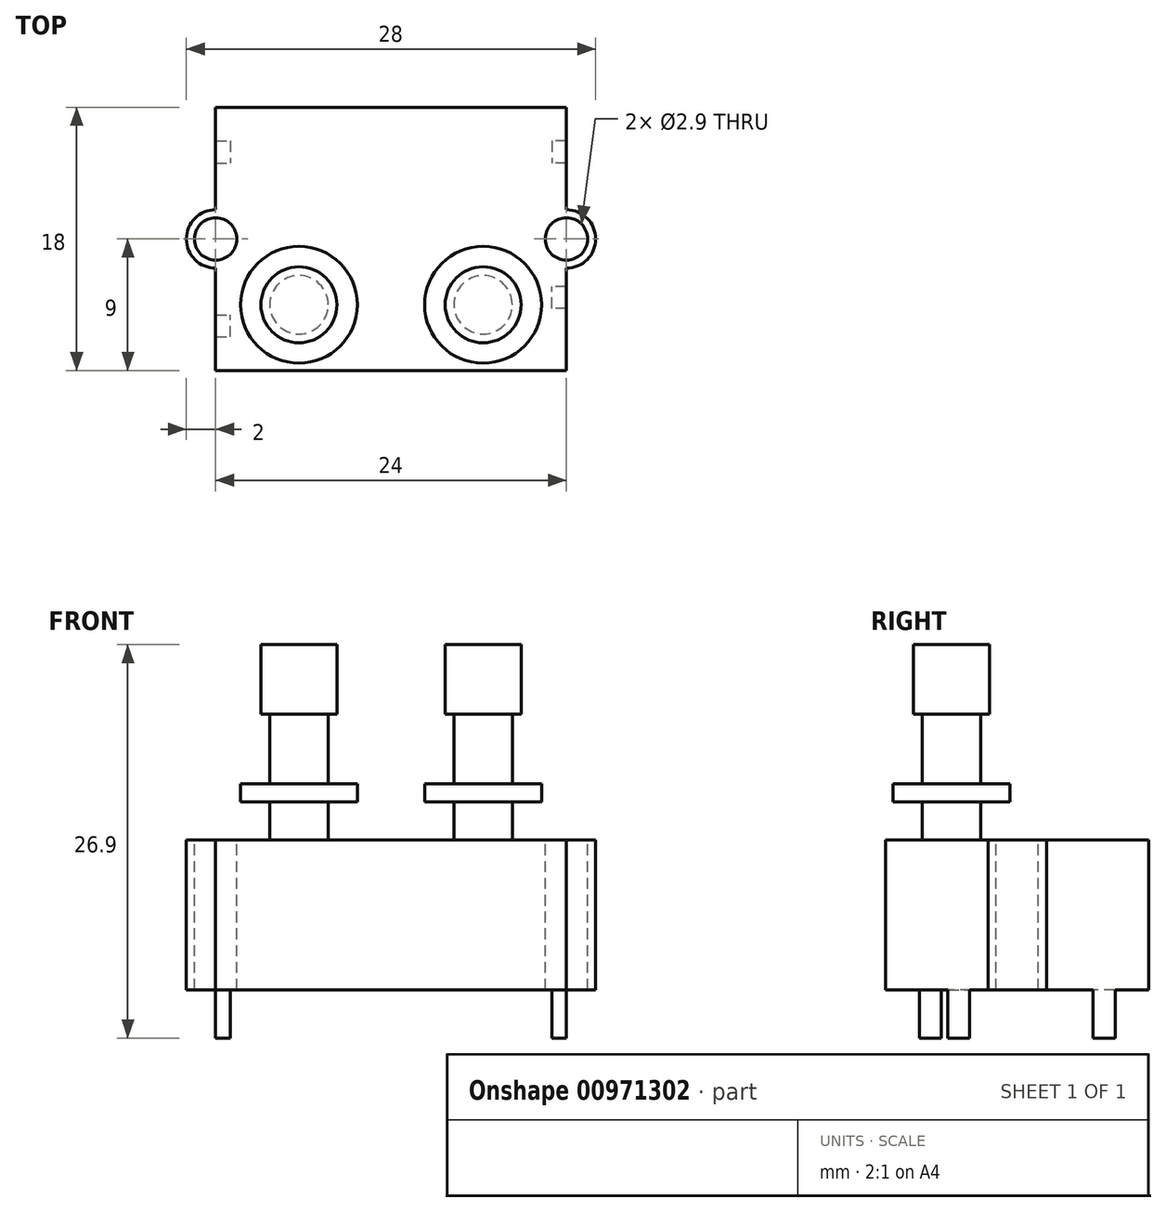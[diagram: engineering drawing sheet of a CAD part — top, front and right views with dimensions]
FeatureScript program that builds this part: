
annotation { "Feature Type Name" : "Feature", "Feature Type Description" : "" }
export const myFeature = defineFeature(function(context is Context, id is Id, definition is map)
    precondition{}
    {
        {
            var Q0;
            Q0=qCreatedBy(makeId("Top.planeOp"),FACE);
            var sketch = newSketch(context, id + "F0", { "sketchPlane" : qUnion([Q0])});
            skLineSegment(sketch, "E0.bottom", {"start": v(-12, 9) * mm, "end": v(12, 9) * mm});
            skLineSegment(sketch, "E0.top", {"start": v(-12, -9) * mm, "end": v(12, -9) * mm});
            skLineSegment(sketch, "E0.left", {"start": v(-12, 9) * mm, "end": v(-12, -9) * mm});
            skLineSegment(sketch, "E0.right", {"start": v(12, 9) * mm, "end": v(12, -9) * mm});
            skSolve(sketch);
        }
        {
            var Q0;
            Q0 = qSketchRegion(id + "F0", true);
            extrude(context, id + "F1", {"entities" : qUnion([Q0]), "depth" : 10.25 * mm, "offsetDistance" : 25 * mm});
        }
        {
            var Q0;
            Q0=makeQuery(id+"F1.opExtrude","CAP_FACE",FACE,{"disambiguationData":[OSD([sQuery(id+"F0.wireOp",EDGE,"E0.bottom"),sQuery(id+"F0.wireOp",EDGE,"E0.top"),sQuery(id+"F0.wireOp",EDGE,"E0.left"),sQuery(id+"F0.wireOp",EDGE,"E0.right")])],"isStart":false});
            var sketch = newSketch(context, id + "F2", { "sketchPlane" : qUnion([Q0])});
            skCircle(sketch, "E1", {"center": v(-6.3, -4.5) * mm, "radius": 2 * mm});
            skCircle(sketch, "E2", {"center": v(6.3, -4.5) * mm, "radius": 2 * mm});
            skSolve(sketch);
        }
        {
            var Q0;
            Q0 = qSketchRegion(id + "F2", true);
            extrude(context, id + "F3", {"entities" : qUnion([Q0]), "operationType" : NewBodyOperationType.ADD, "depth" : 2.6 * mm, "offsetDistance" : 25 * mm});
        }
        {
            var Q0;
            Q0=makeQuery(id+"F3.opExtrude","CAP_FACE",FACE,{"disambiguationData":[OSD([sQuery(id+"F2.wireOp",EDGE,"E1")])],"isStart":false});
            var sketch = newSketch(context, id + "F4", { "sketchPlane" : qUnion([Q0])});
            skCircle(sketch, "E3", {"center": v(-6.3, -4.5) * mm, "radius": 4 * mm});
            skCircle(sketch, "E4", {"center": v(6.3, -4.5) * mm, "radius": 4 * mm});
            skSolve(sketch);
        }
        {
            var Q0;
            Q0=makeQuery(id+"F4.imprint","IMPRINT",FACE,{"disambiguationData":[TD([[makeQuery(id+"F4.imprint","IMPRINT",EDGE,{"derivedFrom":sQuery(id+"F4.wireOp",EDGE,"E4")}),1.0]])]});
            var Q1;
            Q1=makeQuery(id+"F4.imprint","IMPRINT",FACE,{"disambiguationData":[TD([[makeQuery(id+"F4.imprint","IMPRINT",EDGE,{"derivedFrom":makeQuery(id+"F3.opExtrude","CAP_EDGE",EDGE,{"disambiguationData":[OSD([sQuery(id+"F2.wireOp",EDGE,"E1")])],"isStart":false})}),1.0]])]});
            var Q2;
            Q2=makeQuery(id+"F4.imprint","IMPRINT",FACE,{"disambiguationData":[TD([[makeQuery(id+"F4.imprint","IMPRINT",EDGE,{"derivedFrom":sQuery(id+"F4.wireOp",EDGE,"E3")}),1.0]])]});
            extrude(context, id + "F5", {"entities" : qUnion([Q0, Q1, Q2]), "operationType" : NewBodyOperationType.ADD, "depth" : 1.25 * mm, "offsetDistance" : 25 * mm});
        }
        {
            var Q0;
            Q0=makeQuery(id+"F5.opExtrude","CAP_FACE",FACE,{"disambiguationData":[OSD([sQuery(id+"F4.wireOp",EDGE,"E3")])],"isStart":false});
            var sketch = newSketch(context, id + "F6", { "sketchPlane" : qUnion([Q0])});
            skCircle(sketch, "E5", {"center": v(-6.3, -4.5) * mm, "radius": 2 * mm});
            skCircle(sketch, "E6", {"center": v(6.3, -4.5) * mm, "radius": 2 * mm});
            skSolve(sketch);
        }
        {
            var Q0;
            Q0=makeQuery(id+"F6.imprint","IMPRINT",FACE,{"disambiguationData":[TD([[makeQuery(id+"F6.imprint","IMPRINT",EDGE,{"derivedFrom":sQuery(id+"F6.wireOp",EDGE,"E6")}),1.0]])]});
            var Q1;
            Q1=makeQuery(id+"F6.imprint","IMPRINT",FACE,{"disambiguationData":[TD([[makeQuery(id+"F6.imprint","IMPRINT",EDGE,{"derivedFrom":sQuery(id+"F6.wireOp",EDGE,"E5")}),1.0]])]});
            extrude(context, id + "F7", {"entities" : qUnion([Q0, Q1]), "operationType" : NewBodyOperationType.ADD, "depth" : 4.75 * mm, "offsetDistance" : 25 * mm});
        }
        {
            var Q0;
            Q0=makeQuery(id+"F7.opExtrude","CAP_FACE",FACE,{"disambiguationData":[OSD([sQuery(id+"F6.wireOp",EDGE,"E5")])],"isStart":false});
            var sketch = newSketch(context, id + "F8", { "sketchPlane" : qUnion([Q0])});
            skCircle(sketch, "E7", {"center": v(-6.3, -4.5) * mm, "radius": 2.6 * mm});
            skCircle(sketch, "E8", {"center": v(6.3, -4.5) * mm, "radius": 2.6 * mm});
            skSolve(sketch);
        }
        {
            var Q0;
            Q0 = qSketchRegion(id + "F8", true);
            extrude(context, id + "F9", {"entities" : qUnion([Q0]), "operationType" : NewBodyOperationType.ADD, "depth" : 4.75 * mm, "offsetDistance" : 25 * mm});
        }
        {
            var Q0;
            Q0=makeQuery(id+"F1.opExtrude","CAP_FACE",FACE,{"disambiguationData":[OSD([sQuery(id+"F0.wireOp",EDGE,"E0.bottom"),sQuery(id+"F0.wireOp",EDGE,"E0.top"),sQuery(id+"F0.wireOp",EDGE,"E0.left"),sQuery(id+"F0.wireOp",EDGE,"E0.right")])],"isStart":false});
            var sketch = newSketch(context, id + "F10", { "sketchPlane" : qUnion([Q0])});
            skCircle(sketch, "E9", {"center": v(-12, 0) * mm, "radius": 2 * mm});
            skCircle(sketch, "E10", {"center": v(12, 0) * mm, "radius": 2 * mm});
            skSolve(sketch);
        }
        {
            var Q0;
            Q0 = qSketchRegion(id + "F10", true);
            extrude(context, id + "F11", {"entities" : qUnion([Q0]), "operationType" : NewBodyOperationType.ADD, "oppositeDirection" : true, "depth" : 10.25 * mm, "offsetDistance" : 25 * mm});
        }
        {
            var Q0;
            Q0=makeQuery(id+"F11.boolean.opBoolean","MERGE",FACE,{"derivedFrom":[makeQuery(id+"F1.opExtrude","CAP_FACE",FACE,{"disambiguationData":[OSD([sQuery(id+"F0.wireOp",EDGE,"E0.bottom"),sQuery(id+"F0.wireOp",EDGE,"E0.top"),sQuery(id+"F0.wireOp",EDGE,"E0.left"),sQuery(id+"F0.wireOp",EDGE,"E0.right")])],"isStart":false}),makeQuery(id+"F11.opExtrude","CAP_FACE",FACE,{"disambiguationData":[OSD([sQuery(id+"F10.wireOp",EDGE,"E9")])],"isStart":true}),makeQuery(id+"F11.opExtrude","CAP_FACE",FACE,{"disambiguationData":[OSD([sQuery(id+"F10.wireOp",EDGE,"E10")])],"isStart":true})]});
            var sketch = newSketch(context, id + "F12", { "sketchPlane" : qUnion([Q0])});
            skCircle(sketch, "E11", {"center": v(-12, 0) * mm, "radius": 1.45 * mm});
            skCircle(sketch, "E12", {"center": v(12, 0) * mm, "radius": 1.45 * mm});
            skSolve(sketch);
        }
        {
            var Q0;
            Q0 = qSketchRegion(id + "F12", true);
            extrude(context, id + "F13", {"entities" : qUnion([Q0]), "operationType" : NewBodyOperationType.REMOVE, "oppositeDirection" : true, "depth" : 25 * mm, "offsetDistance" : 25 * mm});
        }
        {
            var Q0;
            Q0=makeQuery(id+"F11.boolean.opBoolean","MERGE",FACE,{"derivedFrom":[makeQuery(id+"F1.opExtrude","CAP_FACE",FACE,{"disambiguationData":[OSD([sQuery(id+"F0.wireOp",EDGE,"E0.bottom"),sQuery(id+"F0.wireOp",EDGE,"E0.top"),sQuery(id+"F0.wireOp",EDGE,"E0.left"),sQuery(id+"F0.wireOp",EDGE,"E0.right")])],"isStart":true}),makeQuery(id+"F11.opExtrude","CAP_FACE",FACE,{"disambiguationData":[OSD([sQuery(id+"F10.wireOp",EDGE,"E9")])],"isStart":false}),makeQuery(id+"F11.opExtrude","CAP_FACE",FACE,{"disambiguationData":[OSD([sQuery(id+"F10.wireOp",EDGE,"E10")])],"isStart":false})]});
            var sketch = newSketch(context, id + "F14", { "sketchPlane" : qUnion([Q0])});
            skLineSegment(sketch, "E13.bottom", {"start": v(12, 4.75) * mm, "end": v(11, 4.75) * mm});
            skLineSegment(sketch, "E13.top", {"start": v(12, 3.25) * mm, "end": v(11, 3.25) * mm});
            skLineSegment(sketch, "E13.left", {"start": v(12, 4.75) * mm, "end": v(12, 3.25) * mm});
            skLineSegment(sketch, "E13.right", {"start": v(11, 4.75) * mm, "end": v(11, 3.25) * mm});
            skLineSegment(sketch, "E14.bottom", {"start": v(-12, 6.7) * mm, "end": v(-11, 6.7) * mm});
            skLineSegment(sketch, "E14.top", {"start": v(-12, 5.2) * mm, "end": v(-11, 5.2) * mm});
            skLineSegment(sketch, "E14.left", {"start": v(-12, 6.7) * mm, "end": v(-12, 5.2) * mm});
            skLineSegment(sketch, "E14.right", {"start": v(-11, 6.7) * mm, "end": v(-11, 5.2) * mm});
            skLineSegment(sketch, "E15.bottom", {"start": v(-12, -6.7) * mm, "end": v(-11, -6.7) * mm});
            skLineSegment(sketch, "E15.top", {"start": v(-12, -5.2) * mm, "end": v(-11, -5.2) * mm});
            skLineSegment(sketch, "E15.left", {"start": v(-12, -6.7) * mm, "end": v(-12, -5.2) * mm});
            skLineSegment(sketch, "E15.right", {"start": v(-11, -6.7) * mm, "end": v(-11, -5.2) * mm});
            skLineSegment(sketch, "E16.bottom", {"start": v(12, -6.7) * mm, "end": v(11, -6.7) * mm});
            skLineSegment(sketch, "E16.top", {"start": v(12, -5.2) * mm, "end": v(11, -5.2) * mm});
            skLineSegment(sketch, "E16.left", {"start": v(12, -6.7) * mm, "end": v(12, -5.2) * mm});
            skLineSegment(sketch, "E16.right", {"start": v(11, -6.7) * mm, "end": v(11, -5.2) * mm});
            skSolve(sketch);
        }
        {
            var Q0;
            Q0=makeQuery(id+"F14.imprint","IMPRINT",FACE,{"disambiguationData":[TD([[makeQuery(id+"F14.imprint","IMPRINT",EDGE,{"derivedFrom":sQuery(id+"F14.wireOp",EDGE,"E14.bottom")}),-1.0]])]});
            var Q1;
            Q1=makeQuery(id+"F14.imprint","IMPRINT",FACE,{"disambiguationData":[TD([[makeQuery(id+"F14.imprint","IMPRINT",EDGE,{"derivedFrom":sQuery(id+"F14.wireOp",EDGE,"E15.bottom")}),1.0]])]});
            var Q2;
            Q2=makeQuery(id+"F14.imprint","IMPRINT",FACE,{"disambiguationData":[TD([[makeQuery(id+"F14.imprint","IMPRINT",EDGE,{"derivedFrom":sQuery(id+"F14.wireOp",EDGE,"E16.bottom")}),-1.0]])]});
            var Q3;
            Q3=makeQuery(id+"F14.imprint","IMPRINT",FACE,{"disambiguationData":[TD([[makeQuery(id+"F14.imprint","IMPRINT",EDGE,{"derivedFrom":sQuery(id+"F14.wireOp",EDGE,"E13.bottom")}),1.0]])]});
            extrude(context, id + "F15", {"entities" : qUnion([Q0, Q1, Q2, Q3]), "operationType" : NewBodyOperationType.ADD, "depth" : 3.3 * mm, "offsetDistance" : 25 * mm});
        }
    });
